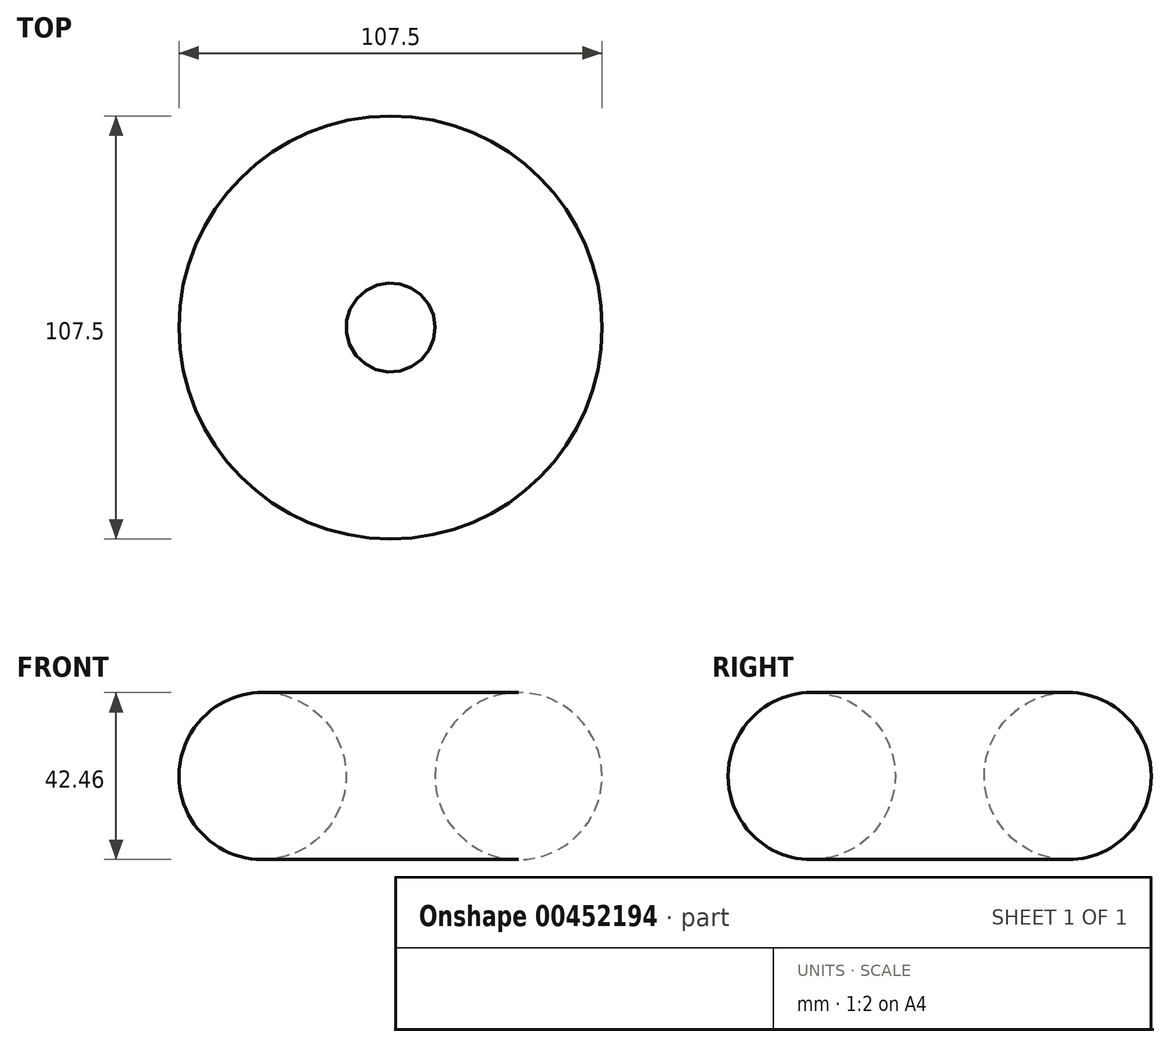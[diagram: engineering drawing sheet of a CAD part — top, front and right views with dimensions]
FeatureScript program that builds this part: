
annotation { "Feature Type Name" : "Feature", "Feature Type Description" : "" }
export const myFeature = defineFeature(function(context is Context, id is Id, definition is map)
    precondition{}
    {
        {
            var Q0;
            Q0=qCreatedBy(makeId("Front.planeOp"),FACE);
            var sketch = newSketch(context, id + "F0", { "sketchPlane" : qUnion([Q0])});
            skCircle(sketch, "E0", {"center": v(32.52, 12.09) * mm, "radius": 21.23 * mm});
            skLineSegment(sketch, "E1", {"start": v(0, 54.97) * mm, "end": v(0, -56.7) * mm});
            skSolve(sketch);
        }
        {
            var Q0;
            Q0 = qSketchRegion(id + "F0", true);
            var Q1;
            Q1=sQuery(id+"F0.wireOp",EDGE,"E1");
            revolve(context, id + "F1", {"entities" : qUnion([Q0]), "axis" : qUnion([Q1]), "revolveType" : RevolveType.FULL});
        }
    });
